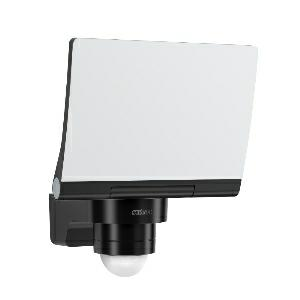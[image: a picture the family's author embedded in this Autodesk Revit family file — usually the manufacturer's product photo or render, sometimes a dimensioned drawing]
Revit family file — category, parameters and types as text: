
# Revit family: xled_pro_240_068110
name_source: partatom
category: Leuchten
revit_build: Autodesk Revit 2016 (Build: 20190508_0715(x64)
units: mm (PartAtom-declared; Revit-internal decimal feet)

## family parameters
Basisbauteil = Fläche
Beim Laden mit Abzugskörper schneiden = Nein
Bemaßung runder Anschluss = Durchmesser verwenden
Gemeinsam genutzt = Nein
Lichtquelle = Nein
Raumberechnungspunkt = Nein
Teiletyp = Normal

## types (1)
- XLED PRO 240 (1 x , 2120 lm, 3000 K)
    Beschreibung = Dimensions (L x W x H): 161 x 180 x 221 mm; Mains power supply: 230 – 240 V / 50 – 60 Hz; Mounting height max.: 6,00 m; Sensor Technology: passive infrared; Output: 20 W; Interconnection: Yes; Switching output 1, resistive: 1000 W; Luminous flux: 2120 lm; Colour temperature: 3000 K; Colour variation LED: SDCM3; Colour Rendering Index CRI: 80-89; With lamp: Yes, STEINEL LED system; Lamp: LED cannot be replaced; LED life expectancy (max. °C): 60000 h; Drop in luminous flux in accordance with LM80: L70B10; LED cooling system: HCMC (High Conductive Magnesium Composite); With motion detector: Yes; Detection angle: 240 °; Angle of aperture: 180 °; Sneak-by guard: Yes; Capability of masking out individual segments: Yes; Reach, radial: r = 3 m (19 m²); Reach, tangential: r = 12 m (302 m²); Photo-cell controller: Yes; Twilight setting: 2 – 1000 lx; Time setting: 10 sec – 15 min; Basic light level function: No; Soft light start: No; Continuous light: selectable; Impact resistance: IK03; IP-rating: IP44; Protection class: II; Ambient temperature: -20 – 40 °C; Housing material: HCMC; Cover material: Plastic, opal; Manufacturer's Warranty: 5 years; Includes corner wall mount: Yes; PU1, net weight: 0,64 kg; Version: warm white black; PU1, EAN: 4007841068110
    Color Rendering = 80-89
    Color Temperature = 3000 K
    Frequency = 60 Hz, 50 Hz
    Height = 221 mm
    Hersteller = Steinel
    Lamp Light Flux = 2120 lm
    Lamp count = 1
    Lampe = 1 x
    Length = 161 mm
    Luminous efficacy = 0 lm/W
    ModVariant = Nein
    Modell = 068110
    Mounting Type = Surface mounted
    Number of Poles = 1
    OnlyDefault = Ja
    Power Factor = 1
    Product Name = XLED PRO 240
    Product group = Sensor-switched indoor light
    ProductGroupID = 30
    Protection Class = Protection class II
    Protection Degree = IP 34
    RlxData = <blob elided: 66969 chars, md5=ab136533>
    Scheinlast = 20 VA
    Socket = socket
    Standby Power = 0 W
    System Light Flux = 0 lm
    System Power = 20 W
    Typenbild = produkt1_068110.jpg
    Typenkommentare = Product without accessories
    URL = http://relux.com
    VarID = ---
    Voltage = 0 V
    Vorgabe-Ansicht = 1800 mm
    Weight = 0.00 kg
    Width = 180 mm  [stored 0.590551 ft]

note: [stored X ft] marks values corroborated as IEEE doubles in the binary element streams (Revit-internal decimal feet)

## geometry (parser evidence)
native form markers: Blend x4, Sweep x16
no freeform markers — native parametric forms only
